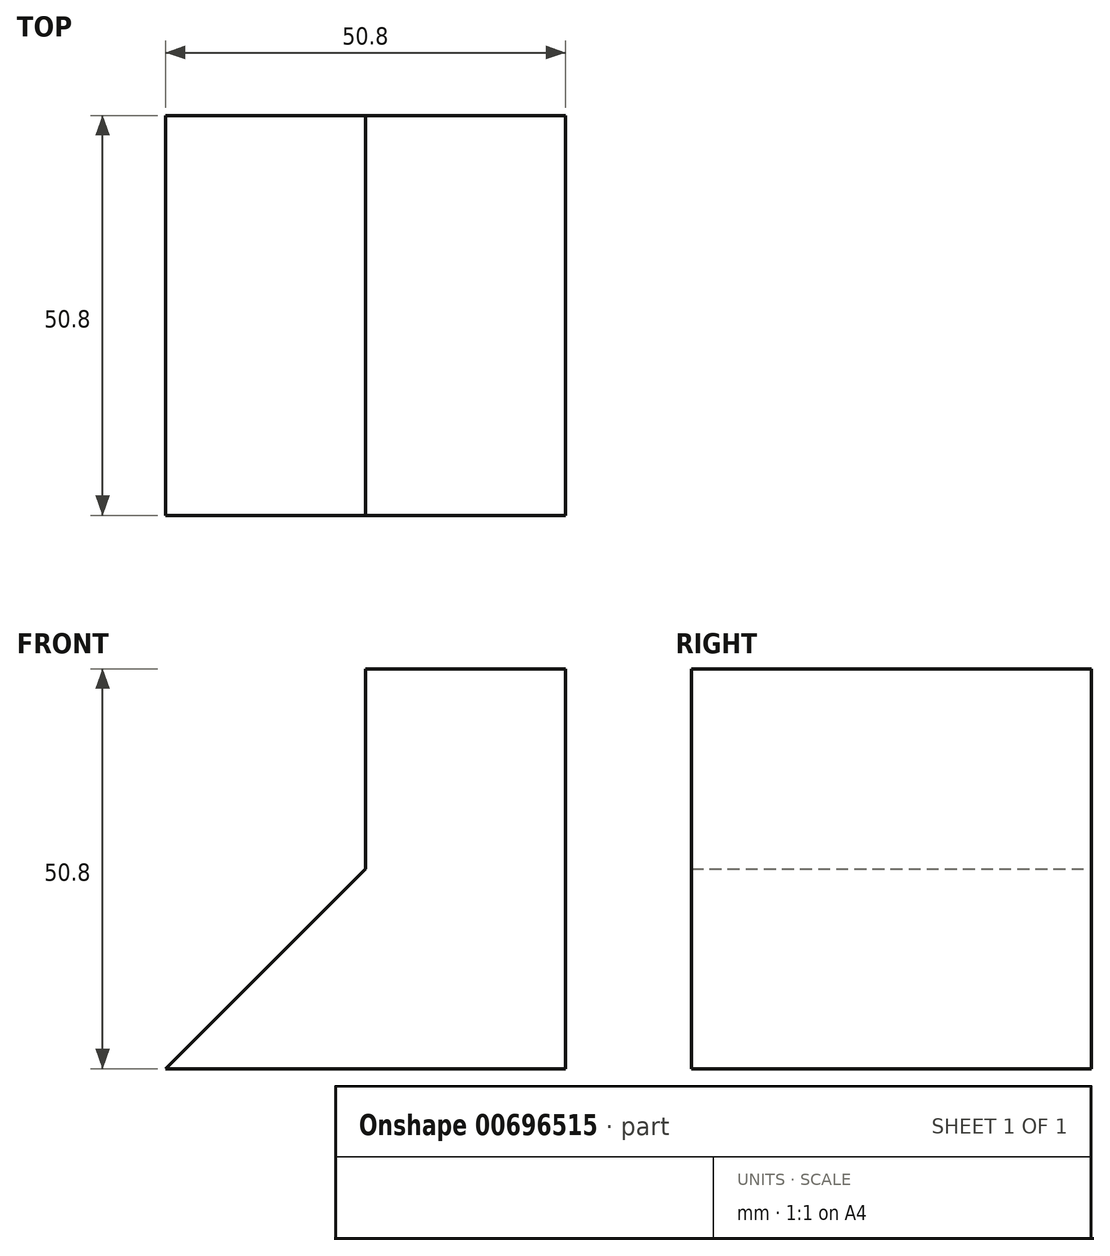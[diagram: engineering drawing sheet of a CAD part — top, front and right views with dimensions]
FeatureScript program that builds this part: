
annotation { "Feature Type Name" : "Feature", "Feature Type Description" : "" }
export const myFeature = defineFeature(function(context is Context, id is Id, definition is map)
    precondition{}
    {
        {
            var Q0;
            Q0=qCreatedBy(makeId("Front.planeOp"),FACE);
            var sketch = newSketch(context, id + "F0", { "sketchPlane" : qUnion([Q0])});
            skLineSegment(sketch, "E0", {"start": v(0, 0) * mm, "end": v(25.4, 0) * mm});
            skLineSegment(sketch, "E1", {"start": v(25.4, 0) * mm, "end": v(25.4, -50.8) * mm});
            skLineSegment(sketch, "E2", {"start": v(25.4, -50.8) * mm, "end": v(-25.4, -50.8) * mm});
            skLineSegment(sketch, "E3", {"start": v(0, 0) * mm, "end": v(0, -25.4) * mm});
            skLineSegment(sketch, "E4", {"start": v(0, -25.4) * mm, "end": v(-25.4, -50.8) * mm});
            skSolve(sketch);
        }
        {
            var Q0;
            Q0 = qSketchRegion(id + "F0", true);
            extrude(context, id + "F1", {"entities" : qUnion([Q0]), "depth" : 50.8 * mm, "offsetDistance" : 25.4 * mm});
        }
    });
